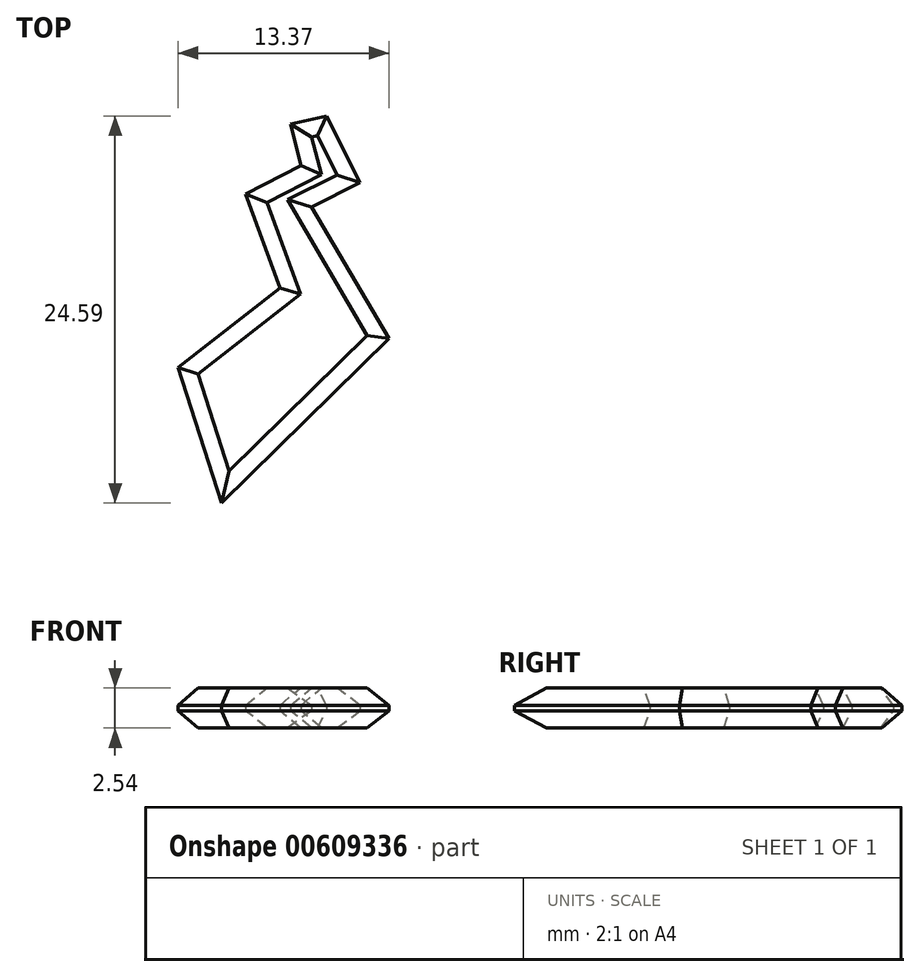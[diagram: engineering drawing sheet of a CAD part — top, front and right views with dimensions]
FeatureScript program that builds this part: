
annotation { "Feature Type Name" : "Feature", "Feature Type Description" : "" }
export const myFeature = defineFeature(function(context is Context, id is Id, definition is map)
    precondition{}
    {
        {
            var Q0;
            Q0=qCreatedBy(makeId("Top.planeOp"),FACE);
            var sketch = newSketch(context, id + "F0", { "sketchPlane" : qUnion([Q0])});
            skLineSegment(sketch, "E0", {"start": v(1.62, 6.31) * mm, "end": v(3.74, 2.07) * mm});
            skLineSegment(sketch, "E1", {"start": v(3.74, 2.07) * mm, "end": v(0.65, 0.53) * mm});
            skLineSegment(sketch, "E2", {"start": v(0.65, 0.53) * mm, "end": v(5.56, -7.82) * mm});
            skLineSegment(sketch, "E3", {"start": v(5.56, -7.82) * mm, "end": v(-5.07, -18.28) * mm});
            skLineSegment(sketch, "E4", {"start": v(-5.07, -18.28) * mm, "end": v(-7.81, -9.68) * mm});
            skLineSegment(sketch, "E5", {"start": v(-7.81, -9.68) * mm, "end": v(-1.35, -4.64) * mm});
            skLineSegment(sketch, "E6", {"start": v(-1.35, -4.64) * mm, "end": v(-3.54, 1.34) * mm});
            skLineSegment(sketch, "E7", {"start": v(-3.54, 1.34) * mm, "end": v(0, 3.15) * mm});
            skLineSegment(sketch, "E8", {"start": v(0, 3.15) * mm, "end": v(-0.69, 5.78) * mm});
            skLineSegment(sketch, "E9", {"start": v(-0.69, 5.78) * mm, "end": v(1.62, 6.31) * mm});
            skSolve(sketch);
        }
        {
            var Q0;
            Q0 = qSketchRegion(id + "F0", true);
            extrude(context, id + "F1", {"entities" : qUnion([Q0]), "depth" : 2.54 * mm, "offsetDistance" : 25.4 * mm});
        }
        {
            var Q0;
            Q0=makeQuery(id+"F1.opExtrude","CAP_FACE",FACE,{"disambiguationData":[OSD([sQuery(id+"F0.wireOp",EDGE,"E0"),sQuery(id+"F0.wireOp",EDGE,"E1"),sQuery(id+"F0.wireOp",EDGE,"E2"),sQuery(id+"F0.wireOp",EDGE,"E3"),sQuery(id+"F0.wireOp",EDGE,"E4"),sQuery(id+"F0.wireOp",EDGE,"E5"),sQuery(id+"F0.wireOp",EDGE,"E6"),sQuery(id+"F0.wireOp",EDGE,"E7"),sQuery(id+"F0.wireOp",EDGE,"E8"),sQuery(id+"F0.wireOp",EDGE,"QGT0l8ke-UHQn-cIBh-o4fl-IA91o7RoRfo2"),sQuery(id+"F0.wireOp",EDGE,"XXXHQey1-qmWY-oByk-SDzq-DqsvN2AKA25O")])],"isStart":false});
            chamfer(context, id + "F2", {"entities" : qUnion([Q0]), "width" : 1.1 * mm, "tangentPropagation" : true});
        }
        {
            var Q0;
            Q0=makeQuery(id+"F1.opExtrude","CAP_FACE",FACE,{"disambiguationData":[OSD([sQuery(id+"F0.wireOp",EDGE,"E0"),sQuery(id+"F0.wireOp",EDGE,"E1"),sQuery(id+"F0.wireOp",EDGE,"E2"),sQuery(id+"F0.wireOp",EDGE,"E3"),sQuery(id+"F0.wireOp",EDGE,"E4"),sQuery(id+"F0.wireOp",EDGE,"E5"),sQuery(id+"F0.wireOp",EDGE,"E6"),sQuery(id+"F0.wireOp",EDGE,"E7"),sQuery(id+"F0.wireOp",EDGE,"E8"),sQuery(id+"F0.wireOp",EDGE,"QGT0l8ke-UHQn-cIBh-o4fl-IA91o7RoRfo2"),sQuery(id+"F0.wireOp",EDGE,"XXXHQey1-qmWY-oByk-SDzq-DqsvN2AKA25O")])],"isStart":true});
            chamfer(context, id + "F3", {"entities" : qUnion([Q0]), "width" : 1.1 * mm, "tangentPropagation" : true});
        }
    });
